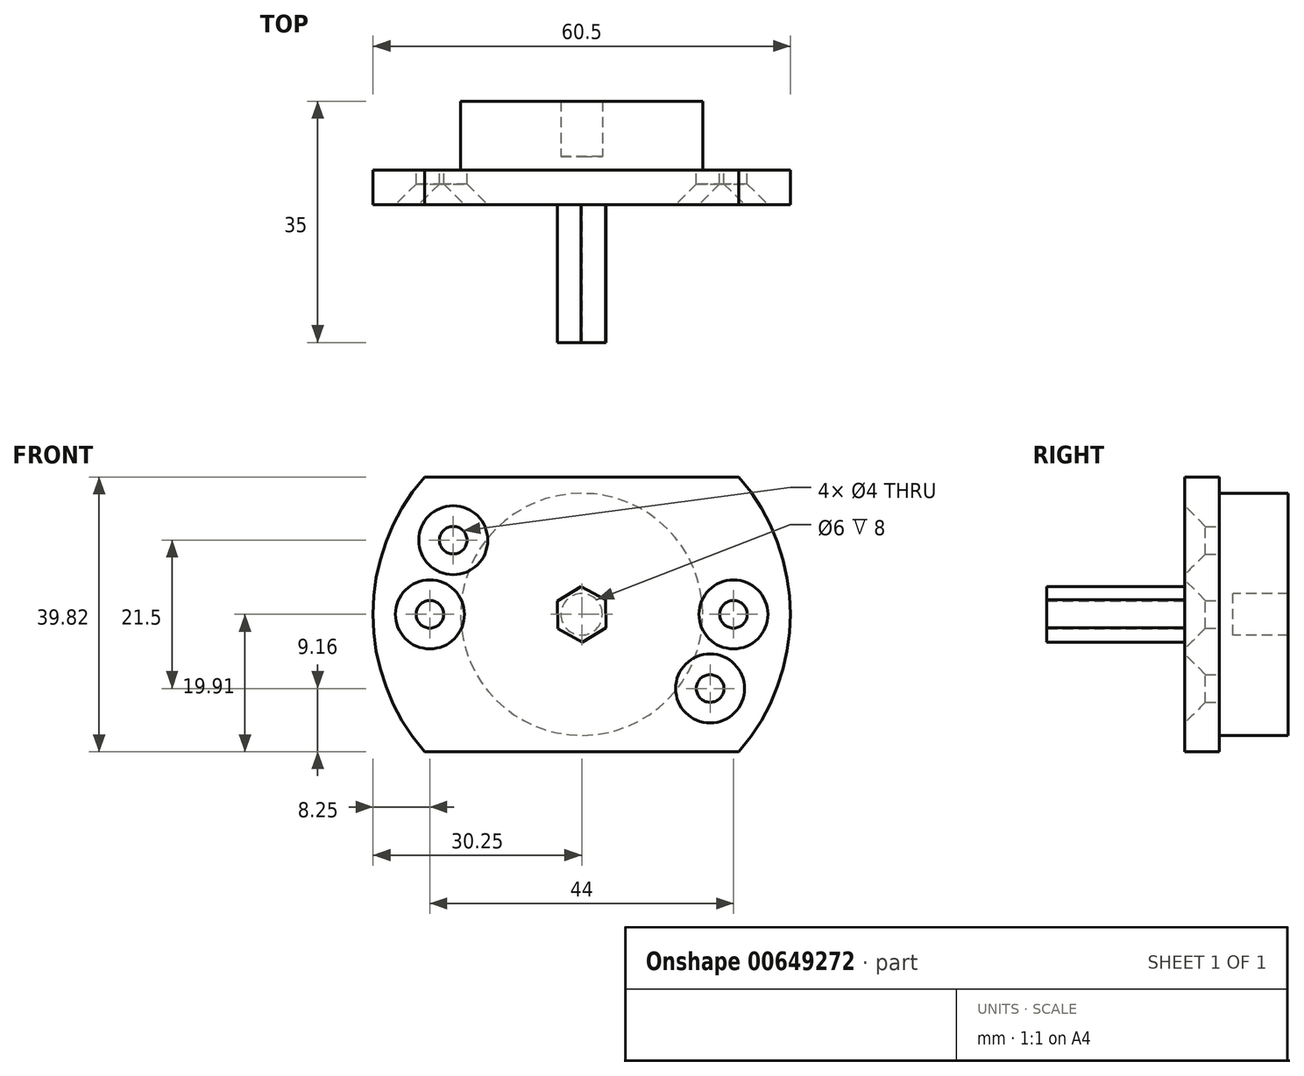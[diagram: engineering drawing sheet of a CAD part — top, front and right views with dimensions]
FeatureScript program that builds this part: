
annotation { "Feature Type Name" : "Feature", "Feature Type Description" : "" }
export const myFeature = defineFeature(function(context is Context, id is Id, definition is map)
    precondition{}
    {
        {
            var Q0;
            Q0=qCreatedBy(makeId("Front.planeOp"),FACE);
            var sketch = newSketch(context, id + "F0", { "sketchPlane" : qUnion([Q0])});
            skCircle(sketch, "E0", {"center": v(0, 0) * mm, "radius": 30.25 * mm});
            skCircle(sketch, "E1.0", {"center": v(0, 0) * mm, "radius": 17.55 * mm});
            skCircle(sketch, "E2", {"center": v(-22, 0) * mm, "radius": 2 * mm});
            skCircle(sketch, "E3", {"center": v(22, 0) * mm, "radius": 2 * mm});
            skCircle(sketch, "E4", {"center": v(-18.62, 10.75) * mm, "radius": 2 * mm});
            skCircle(sketch, "E5", {"center": v(18.62, -10.75) * mm, "radius": 2 * mm});
            skLineSegment(sketch, "E6", {"start": v(0, 0) * mm, "end": v(-18.62, 10.75) * mm});
            skLineSegment(sketch, "E7", {"start": v(0, 0) * mm, "end": v(8.77, 15.2) * mm});
            skCircle(sketch, "E8.cCircle", {"center": v(0, 0) * mm, "radius": 3.5 * mm, "construction": true});
            skLineSegment(sketch, "E8.0", {"start": v(3.54, -1.95) * mm, "end": v(0.08, -4.04) * mm});
            skLineSegment(sketch, "E8.1", {"start": v(0.08, -4.04) * mm, "end": v(-3.46, -2.1) * mm});
            skLineSegment(sketch, "E8.2", {"start": v(-3.46, -2.1) * mm, "end": v(-3.54, 1.95) * mm});
            skLineSegment(sketch, "E8.3", {"start": v(-3.54, 1.95) * mm, "end": v(-0.08, 4.04) * mm});
            skLineSegment(sketch, "E8.4", {"start": v(-0.08, 4.04) * mm, "end": v(3.46, 2.1) * mm});
            skLineSegment(sketch, "E8.5", {"start": v(3.46, 2.1) * mm, "end": v(3.54, -1.95) * mm});
            skPoint(sketch, "E8.0.midPoint", {"position": v(1.81, -3) * mm});
            skLineSegment(sketch, "E9", {"start": v(-22.77, -19.91) * mm, "end": v(22.77, -19.91) * mm});
            skLineSegment(sketch, "E10", {"start": v(0, 0) * mm, "end": v(2.28, 0) * mm});
            skLineSegment(sketch, "E11.MirrorCS", {"start": v(-22.77, 19.91) * mm, "end": v(22.77, 19.91) * mm});
            skCircle(sketch, "E12", {"center": v(0, 0) * mm, "radius": 3 * mm});
            skSolve(sketch);
        }
        {
            var Q0;
            Q0=makeQuery(id+"F0.imprint","IMPRINT",FACE,{"disambiguationData":[TD([[makeQuery(id+"F0.imprint","IMPRINT",EDGE,{"derivedFrom":sQuery(id+"F0.wireOp",EDGE,"E2")}),-1.0]])]});
            var Q1;
            Q1=makeQuery(id+"F0.imprint","IMPRINT",FACE,{"disambiguationData":[TD([[makeQuery(id+"F0.imprint","IMPRINT",EDGE,{"derivedFrom":sQuery(id+"F0.wireOp",EDGE,"E8.0")}),1.0]])]});
            var Q2;
            {var subQ5=sQuery(id+"F0.wireOp",EDGE,"E7");var subQ6=sQuery(id+"F0.wireOp",EDGE,"E1.0");var subQ7=makeQuery(id+"F0.imprint","INTERSECT",VERTEX,{"derivedFrom":[subQ6,subQ5]});Q2=makeQuery(id+"F0.imprint","IMPRINT",FACE,{"disambiguationData":[TD([[makeQuery(id+"F0.imprint","IMPRINT",EDGE,{"disambiguationData":[TD([[subQ7,-1.0]])],"derivedFrom":subQ6}),1.0]])]});}
            var Q3;
            Q3=makeQuery(id+"F0.imprint","IMPRINT",FACE,{"disambiguationData":[TD([[makeQuery(id+"F0.imprint","IMPRINT",EDGE,{"derivedFrom":sQuery(id+"F0.wireOp",EDGE,"E8.0")}),-1.0]])]});
            var Q4;
            {var subQ0=sQuery(id+"F0.wireOp",EDGE,"E7");var subQ1=sQuery(id+"F0.wireOp",EDGE,"E6");var subQ2=makeQuery(id+"F0.imprint","INTERSECT",VERTEX,{"derivedFrom":[subQ1,subQ0]});Q4=makeQuery(id+"F0.imprint","IMPRINT",FACE,{"disambiguationData":[TD([[makeQuery(id+"F0.imprint","IMPRINT",EDGE,{"disambiguationData":[TD([[subQ2,-1.0]])],"derivedFrom":subQ1}),-1.0]])]});}
            var Q5;
            {var subQ3=sQuery(id+"F0.wireOp",EDGE,"E6");var subQ5=sQuery(id+"F0.wireOp",EDGE,"E12");var subQ9=makeQuery(id+"F0.imprint","INTERSECT",VERTEX,{"derivedFrom":[subQ3,subQ5]});Q5=makeQuery(id+"F0.imprint","IMPRINT",FACE,{"disambiguationData":[TD([[makeQuery(id+"F0.imprint","IMPRINT",EDGE,{"disambiguationData":[TD([[subQ9,-1.0]])],"derivedFrom":subQ3}),-1.0]])]});}
            var Q6;
            {var subQ0=sQuery(id+"F0.wireOp",EDGE,"E7");var subQ1=sQuery(id+"F0.wireOp",EDGE,"E6");var subQ2=makeQuery(id+"F0.imprint","INTERSECT",VERTEX,{"derivedFrom":[subQ1,subQ0]});Q6=makeQuery(id+"F0.imprint","IMPRINT",FACE,{"disambiguationData":[TD([[makeQuery(id+"F0.imprint","IMPRINT",EDGE,{"disambiguationData":[TD([[subQ2,-1.0]])],"derivedFrom":subQ1}),1.0]])]});}
            extrude(context, id + "F1", {"entities" : qUnion([Q0, Q1, Q2, Q3, Q4, Q5, Q6]), "depth" : 5 * mm, "offsetDistance" : 25 * mm});
        }
        {
            var Q0;
            {var subQ0=sQuery(id+"F0.wireOp",EDGE,"E7");var subQ1=sQuery(id+"F0.wireOp",EDGE,"E6");var subQ2=makeQuery(id+"F0.imprint","INTERSECT",VERTEX,{"derivedFrom":[subQ1,subQ0]});Q0=makeQuery(id+"F0.imprint","IMPRINT",FACE,{"disambiguationData":[TD([[makeQuery(id+"F0.imprint","IMPRINT",EDGE,{"disambiguationData":[TD([[subQ2,-1.0]])],"derivedFrom":subQ1}),-1.0]])]});}
            var Q1;
            {var subQ0=sQuery(id+"F0.wireOp",EDGE,"E7");var subQ1=sQuery(id+"F0.wireOp",EDGE,"E6");var subQ2=makeQuery(id+"F0.imprint","INTERSECT",VERTEX,{"derivedFrom":[subQ1,subQ0]});Q1=makeQuery(id+"F0.imprint","IMPRINT",FACE,{"disambiguationData":[TD([[makeQuery(id+"F0.imprint","IMPRINT",EDGE,{"disambiguationData":[TD([[subQ2,-1.0]])],"derivedFrom":subQ1}),1.0]])]});}
            var Q2;
            Q2=makeQuery(id+"F0.imprint","IMPRINT",FACE,{"disambiguationData":[TD([[makeQuery(id+"F0.imprint","IMPRINT",EDGE,{"derivedFrom":sQuery(id+"F0.wireOp",EDGE,"E8.0")}),-1.0]])]});
            var Q3;
            {var subQ3=sQuery(id+"F0.wireOp",EDGE,"E6");var subQ5=sQuery(id+"F0.wireOp",EDGE,"E12");var subQ9=makeQuery(id+"F0.imprint","INTERSECT",VERTEX,{"derivedFrom":[subQ3,subQ5]});Q3=makeQuery(id+"F0.imprint","IMPRINT",FACE,{"disambiguationData":[TD([[makeQuery(id+"F0.imprint","IMPRINT",EDGE,{"disambiguationData":[TD([[subQ9,-1.0]])],"derivedFrom":subQ3}),-1.0]])]});}
            var Q4;
            Q4=makeQuery(id+"F0.imprint","IMPRINT",FACE,{"disambiguationData":[TD([[makeQuery(id+"F0.imprint","IMPRINT",EDGE,{"derivedFrom":sQuery(id+"F0.wireOp",EDGE,"E8.0")}),1.0]])]});
            var Q5;
            {var subQ5=sQuery(id+"F0.wireOp",EDGE,"E7");var subQ6=sQuery(id+"F0.wireOp",EDGE,"E1.0");var subQ7=makeQuery(id+"F0.imprint","INTERSECT",VERTEX,{"derivedFrom":[subQ6,subQ5]});Q5=makeQuery(id+"F0.imprint","IMPRINT",FACE,{"disambiguationData":[TD([[makeQuery(id+"F0.imprint","IMPRINT",EDGE,{"disambiguationData":[TD([[subQ7,-1.0]])],"derivedFrom":subQ6}),1.0]])]});}
            extrude(context, id + "F2", {"entities" : qUnion([Q0, Q1, Q2, Q3, Q4, Q5]), "operationType" : NewBodyOperationType.ADD, "depth" : 5 * mm, "offsetDistance" : 25 * mm, "hasSecondDirection" : true, "secondDirectionOppositeDirection" : true, "secondDirectionDepth" : 10 * mm});
        }
        {
            var Q0;
            Q0=makeQuery(id+"F1.opExtrude","CAP_EDGE",EDGE,{"disambiguationData":[OSD([sQuery(id+"F0.wireOp",EDGE,"E4")])],"isStart":false});
            var Q1;
            Q1=makeQuery(id+"F1.opExtrude","CAP_EDGE",EDGE,{"disambiguationData":[OSD([sQuery(id+"F0.wireOp",EDGE,"E5")])],"isStart":false});
            var Q2;
            Q2=makeQuery(id+"F1.opExtrude","CAP_EDGE",EDGE,{"disambiguationData":[OSD([sQuery(id+"F0.wireOp",EDGE,"E3")])],"isStart":false});
            var Q3;
            Q3=makeQuery(id+"F1.opExtrude","CAP_EDGE",EDGE,{"disambiguationData":[OSD([sQuery(id+"F0.wireOp",EDGE,"E2")])],"isStart":false});
            chamfer(context, id + "F3", {"entities" : qUnion([Q0, Q1, Q2, Q3]), "width" : 3 * mm, "tangentPropagation" : true});
        }
        {
            var Q0;
            {var subQ3=sQuery(id+"F0.wireOp",EDGE,"E6");var subQ5=sQuery(id+"F0.wireOp",EDGE,"E12");var subQ9=makeQuery(id+"F0.imprint","INTERSECT",VERTEX,{"derivedFrom":[subQ3,subQ5]});Q0=makeQuery(id+"F0.imprint","IMPRINT",FACE,{"disambiguationData":[TD([[makeQuery(id+"F0.imprint","IMPRINT",EDGE,{"disambiguationData":[TD([[subQ9,-1.0]])],"derivedFrom":subQ3}),-1.0]])]});}
            var Q1;
            Q1=makeQuery(id+"F0.imprint","IMPRINT",FACE,{"disambiguationData":[TD([[makeQuery(id+"F0.imprint","IMPRINT",EDGE,{"derivedFrom":sQuery(id+"F0.wireOp",EDGE,"E8.0")}),-1.0]])]});
            var Q2;
            {var subQ0=sQuery(id+"F0.wireOp",EDGE,"E7");var subQ1=sQuery(id+"F0.wireOp",EDGE,"E6");var subQ2=makeQuery(id+"F0.imprint","INTERSECT",VERTEX,{"derivedFrom":[subQ1,subQ0]});Q2=makeQuery(id+"F0.imprint","IMPRINT",FACE,{"disambiguationData":[TD([[makeQuery(id+"F0.imprint","IMPRINT",EDGE,{"disambiguationData":[TD([[subQ2,-1.0]])],"derivedFrom":subQ1}),1.0]])]});}
            var Q3;
            {var subQ0=sQuery(id+"F0.wireOp",EDGE,"E7");var subQ1=sQuery(id+"F0.wireOp",EDGE,"E6");var subQ2=makeQuery(id+"F0.imprint","INTERSECT",VERTEX,{"derivedFrom":[subQ1,subQ0]});Q3=makeQuery(id+"F0.imprint","IMPRINT",FACE,{"disambiguationData":[TD([[makeQuery(id+"F0.imprint","IMPRINT",EDGE,{"disambiguationData":[TD([[subQ2,-1.0]])],"derivedFrom":subQ1}),-1.0]])]});}
            extrude(context, id + "F4", {"entities" : qUnion([Q0, Q1, Q2, Q3]), "operationType" : NewBodyOperationType.ADD, "depth" : 25 * mm, "offsetDistance" : 25 * mm});
        }
        {
            var Q0;
            {var subQ0=sQuery(id+"F0.wireOp",EDGE,"E7");var subQ1=sQuery(id+"F0.wireOp",EDGE,"E6");var subQ2=makeQuery(id+"F0.imprint","INTERSECT",VERTEX,{"derivedFrom":[subQ1,subQ0]});Q0=makeQuery(id+"F0.imprint","IMPRINT",FACE,{"disambiguationData":[TD([[makeQuery(id+"F0.imprint","IMPRINT",EDGE,{"disambiguationData":[TD([[subQ2,-1.0]])],"derivedFrom":subQ1}),1.0]])]});}
            var Q1;
            {var subQ0=sQuery(id+"F0.wireOp",EDGE,"E7");var subQ1=sQuery(id+"F0.wireOp",EDGE,"E6");var subQ2=makeQuery(id+"F0.imprint","INTERSECT",VERTEX,{"derivedFrom":[subQ1,subQ0]});Q1=makeQuery(id+"F0.imprint","IMPRINT",FACE,{"disambiguationData":[TD([[makeQuery(id+"F0.imprint","IMPRINT",EDGE,{"disambiguationData":[TD([[subQ2,-1.0]])],"derivedFrom":subQ1}),-1.0]])]});}
            extrude(context, id + "F5", {"entities" : qUnion([Q0, Q1]), "operationType" : NewBodyOperationType.REMOVE, "oppositeDirection" : true, "depth" : 10 * mm, "offsetDistance" : 25 * mm, "hasSecondDirection" : true, "secondDirectionOppositeDirection" : false, "secondDirectionDepth" : -2 * mm});
        }
    });
